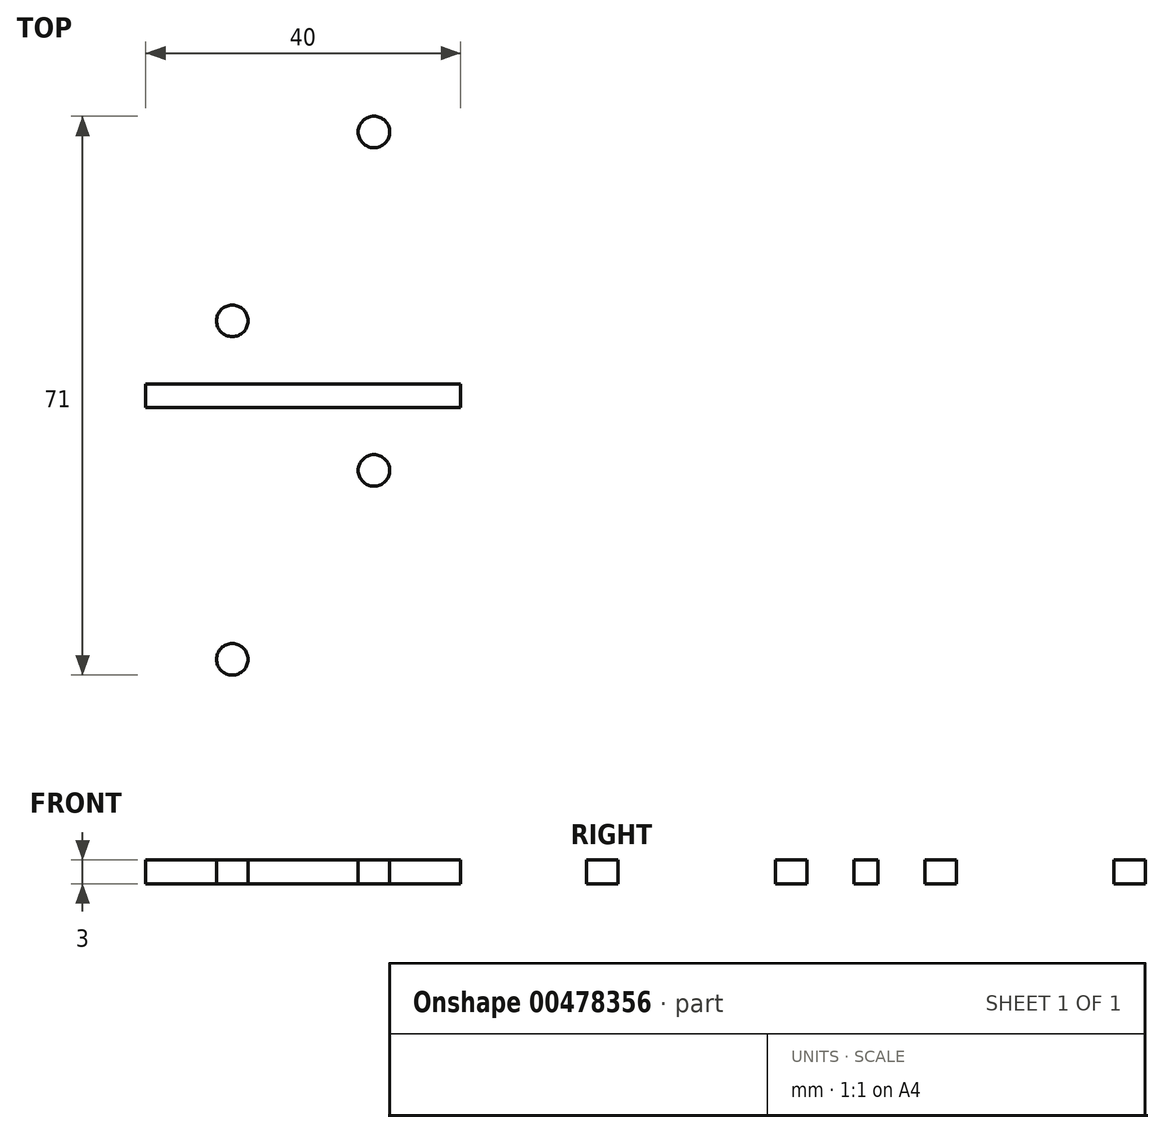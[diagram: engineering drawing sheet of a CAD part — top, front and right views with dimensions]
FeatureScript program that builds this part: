
annotation { "Feature Type Name" : "Feature", "Feature Type Description" : "" }
export const myFeature = defineFeature(function(context is Context, id is Id, definition is map)
    precondition{}
    {
        {
            var Q0;
            Q0=qCreatedBy(makeId("Top.planeOp"),FACE);
            var sketch = newSketch(context, id + "F0", { "sketchPlane" : qUnion([Q0])});
            skLineSegment(sketch, "E0.bottom", {"start": v(20, 50) * mm, "end": v(-20, 50) * mm});
            skLineSegment(sketch, "E0.top", {"start": v(20, -50) * mm, "end": v(-20, -50) * mm});
            skLineSegment(sketch, "E0.left", {"start": v(20, 50) * mm, "end": v(20, -50) * mm});
            skLineSegment(sketch, "E0.right", {"start": v(-20, 50) * mm, "end": v(-20, -50) * mm});
            skPoint(sketch, "E0.middle", {"position": v(0, 0) * mm});
            skSolve(sketch);
        }
        {
            var Q0;
            Q0=makeQuery(id+"F0.imprint","IMPRINT",FACE,{"disambiguationData":[TD([[makeQuery(id+"F0.imprint","IMPRINT",EDGE,{"derivedFrom":sQuery(id+"F0.wireOp",EDGE,"E0.bottom")}),1.0]])]});
            extrude(context, id + "F1", {"entities" : qUnion([Q0]), "endBound" : BoundingType.SYMMETRIC, "depth" : 3 * mm});
        }
        {
            var Q0;
            Q0=makeQuery(id+"F1.opExtrude","CAP_FACE",FACE,{"disambiguationData":[OSD([sQuery(id+"F0.wireOp",EDGE,"E0.bottom"),sQuery(id+"F0.wireOp",EDGE,"E0.top"),sQuery(id+"F0.wireOp",EDGE,"E0.left"),sQuery(id+"F0.wireOp",EDGE,"E0.right")])],"isStart":false});
            var sketch = newSketch(context, id + "F2", { "sketchPlane" : qUnion([Q0])});
            skCircle(sketch, "E1", {"center": v(-9, 33.5) * mm, "radius": 2 * mm});
            skCircle(sketch, "E2.MirrorC", {"center": v(9, 33.5) * mm, "radius": 2 * mm});
            skLineSegment(sketch, "E3", {"start": v(-20, 1.5) * mm, "end": v(20, 1.5) * mm});
            skLineSegment(sketch, "E4.MirrorCS", {"start": v(-20, -1.5) * mm, "end": v(20, -1.5) * mm});
            skLineSegment(sketch, "E5", {"start": v(-20, 21.5) * mm, "end": v(20, 21.5) * mm});
            skCircle(sketch, "E6.MirrorC", {"center": v(-9, 9.5) * mm, "radius": 2 * mm});
            skCircle(sketch, "E7.MirrorC", {"center": v(9, 9.5) * mm, "radius": 2 * mm});
            skCircle(sketch, "E8.MirrorC", {"center": v(-9, -9.5) * mm, "radius": 2 * mm});
            skCircle(sketch, "E9.MirrorC", {"center": v(9, -9.5) * mm, "radius": 2 * mm});
            skCircle(sketch, "E10.MirrorC", {"center": v(9, -33.5) * mm, "radius": 2 * mm});
            skCircle(sketch, "E11.MirrorC", {"center": v(-9, -33.5) * mm, "radius": 2 * mm});
            skSolve(sketch);
        }
        {
            var Q0;
            Q0=makeQuery(id+"F2.imprint","IMPRINT",FACE,{"disambiguationData":[TD([[makeQuery(id+"F2.imprint","IMPRINT",EDGE,{"derivedFrom":sQuery(id+"F2.wireOp",EDGE,"E1")}),1.0]])]});
            var Q1;
            Q1=makeQuery(id+"F2.imprint","IMPRINT",FACE,{"disambiguationData":[TD([[makeQuery(id+"F2.imprint","IMPRINT",EDGE,{"derivedFrom":sQuery(id+"F2.wireOp",EDGE,"E2.MirrorC")}),-1.0]])]});
            var Q2;
            Q2=makeQuery(id+"F2.imprint","IMPRINT",FACE,{"disambiguationData":[TD([[makeQuery(id+"F2.imprint","IMPRINT",EDGE,{"derivedFrom":sQuery(id+"F2.wireOp",EDGE,"E6.MirrorC")}),-1.0]])]});
            var Q3;
            Q3=makeQuery(id+"F2.imprint","IMPRINT",FACE,{"disambiguationData":[TD([[makeQuery(id+"F2.imprint","IMPRINT",EDGE,{"derivedFrom":sQuery(id+"F2.wireOp",EDGE,"E7.MirrorC")}),1.0]])]});
            var Q4;
            Q4=makeQuery(id+"F2.imprint","IMPRINT",FACE,{"disambiguationData":[TD([[makeQuery(id+"F2.imprint","IMPRINT",EDGE,{"derivedFrom":sQuery(id+"F2.wireOp",EDGE,"E8.MirrorC")}),1.0]])]});
            var Q5;
            Q5=makeQuery(id+"F2.imprint","IMPRINT",FACE,{"disambiguationData":[TD([[makeQuery(id+"F2.imprint","IMPRINT",EDGE,{"derivedFrom":sQuery(id+"F2.wireOp",EDGE,"E9.MirrorC")}),-1.0]])]});
            var Q6;
            Q6=makeQuery(id+"F2.imprint","IMPRINT",FACE,{"disambiguationData":[TD([[makeQuery(id+"F2.imprint","IMPRINT",EDGE,{"derivedFrom":sQuery(id+"F2.wireOp",EDGE,"E11.MirrorC")}),-1.0]])]});
            var Q7;
            Q7=makeQuery(id+"F2.imprint","IMPRINT",FACE,{"disambiguationData":[TD([[makeQuery(id+"F2.imprint","IMPRINT",EDGE,{"derivedFrom":sQuery(id+"F2.wireOp",EDGE,"E10.MirrorC")}),1.0]])]});
            extrude(context, id + "F3", {"entities" : qUnion([Q0, Q1, Q2, Q3, Q4, Q5, Q6, Q7]), "operationType" : NewBodyOperationType.REMOVE, "endBound" : BoundingType.THROUGH_ALL, "oppositeDirection" : true, "depth" : 25 * mm});
        }
    });
